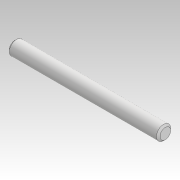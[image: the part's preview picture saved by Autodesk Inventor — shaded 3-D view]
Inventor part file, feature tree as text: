
AUTODESK INVENTOR PART (.ipt)
format: ipt  version: 2020 (Build 240168000, 168)  size: 85,504 bytes
history: native  units: mm
features: revolve x1, sketch x1
ambient origin geometry x8: Origin, YZ Plane, XZ Plane, XY Plane, X Axis, Y Axis, Z Axis, Center Point
bodies: Solid1 (feature_tree)
feature tree (2):
  revolve  "Revolution1"  Angle=135.0deg
  sketch  "Sketch1"  dims[d0=4.0mm d1=135.0deg d2=1.0mm d3=85.0mm d4=90.0deg]
